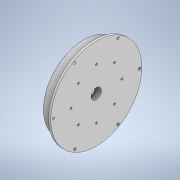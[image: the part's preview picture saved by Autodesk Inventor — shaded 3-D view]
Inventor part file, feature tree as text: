
AUTODESK INVENTOR PART (.ipt)
format: ipt  version: 2021 (Build 250183000, 183)  size: 204,800 bytes
history: native  units: mm
features: sketch x3, chamfer x2, hole x2, revolve x1, pattern_circular x1, projected_geometry x1
ambient origin geometry x8: Origin, YZ Plane, XZ Plane, XY Plane, X Axis, Y Axis, Z Axis, Center Point
bodies: Solid1 (feature_tree)
feature tree (10):
  revolve  "Revolution1"  Angle=90.0deg
  chamfer  "Chamfer1"  Distance=1.0mm Angle=45.0deg
  hole  "Hole1"  [1 undecoded]
  pattern_circular  "Circular Pattern1"  [2 undecoded]
  chamfer  "Chamfer2"  Distance=6.0mm
  hole  "Hole2"  [1 undecoded]
  sketch  "Sketch1"  dims[d7=8.5mm d11=90.0deg]
  sketch  "Sketch2"  dims[d15=1.5mm]
  projected_geometry  "Projected Loop1"
  sketch  "Sketch3"  dims[d18=1.625mm d19=1.0mm d20=2.0mm d21=45.0deg d23=13.1mm d25=64.0mm d26=6.0mm d27=50.0mm d28=4.92233mm d29=3.5mm d30=4.0mm d31=9.0mm d33=4.5mm d34=4.5mm d35=4.5mm d36=8.0mm d37=9.4mm d38=2.0mm d39=90.0deg d40=8.0mm d41=20.594885mm d42=60.0mm d43=360.0deg d45=0.4mm d46=2.0mm d47=45.0deg d48=91.0mm d49=80.0mm d51=360.0deg d53=3.242mm d54=8.0mm d55=4.0mm d56=2.0mm d57=90.0deg d58=11.8mm d59=20.594885mm]
note: 4 required parameter values undecoded (feature->parameter linkage not recoverable at this tier; creation-order binding heuristic only, values carry confidence <= 0.55)
